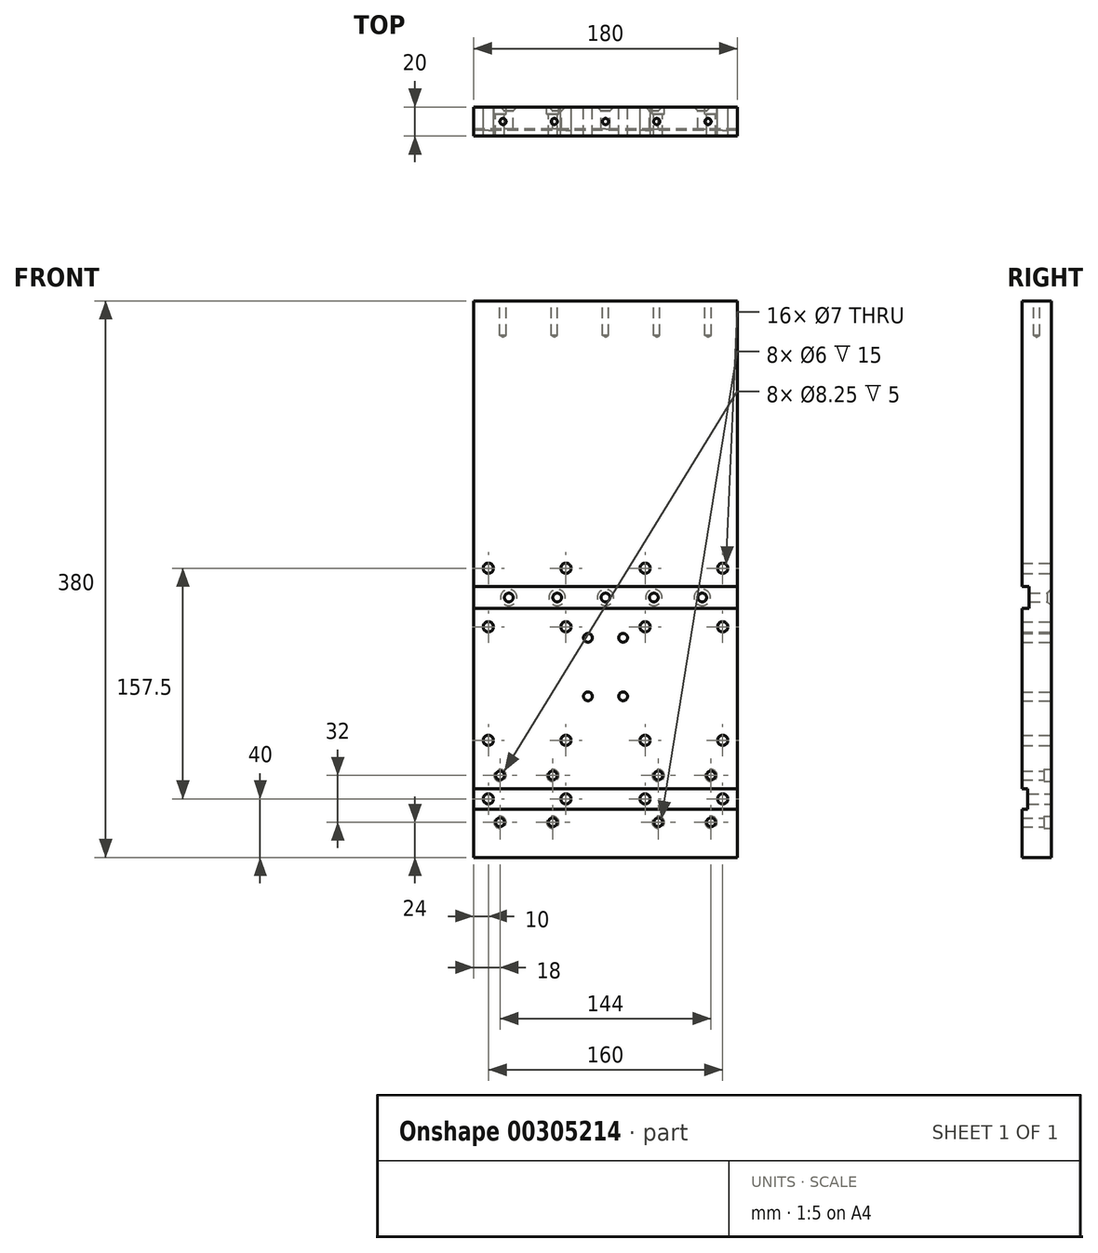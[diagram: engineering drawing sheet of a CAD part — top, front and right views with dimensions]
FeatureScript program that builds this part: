
annotation { "Feature Type Name" : "Feature", "Feature Type Description" : "" }
export const myFeature = defineFeature(function(context is Context, id is Id, definition is map)
    precondition{}
    {
        {
            var Q0;
            Q0=qCreatedBy(makeId("Right.planeOp"),FACE);
            var sketch = newSketch(context, id + "F0", { "sketchPlane" : qUnion([Q0])});
            skLineSegment(sketch, "E0.bottom", {"start": v(0, 0) * mm, "end": v(0, 0) * mm});
            skLineSegment(sketch, "E1.bottom", {"start": v(0, 0) * mm, "end": v(20, 0) * mm});
            skLineSegment(sketch, "E1.top", {"start": v(0, 400) * mm, "end": v(20, 400) * mm});
            skLineSegment(sketch, "E1.left", {"start": v(0, 0) * mm, "end": v(0, 170) * mm});
            skLineSegment(sketch, "E1.right", {"start": v(20, 0) * mm, "end": v(20, 400) * mm});
            skLineSegment(sketch, "E2.0", {"start": v(0, 170) * mm, "end": v(5, 170) * mm});
            skLineSegment(sketch, "E3.0", {"start": v(0, 185) * mm, "end": v(5, 185) * mm});
            skLineSegment(sketch, "E4.0", {"start": v(5, 170) * mm, "end": v(5, 185) * mm});
            skLineSegment(sketch, "E5.trimOffspring", {"start": v(0, 185) * mm, "end": v(0, 400) * mm});
            skSolve(sketch);
        }
        {
            var Q0;
            Q0=makeQuery(id+"F0.imprint","IMPRINT",FACE,{"disambiguationData":[TD([[makeQuery(id+"F0.imprint","IMPRINT",EDGE,{"derivedFrom":sQuery(id+"F0.wireOp",EDGE,"E1.bottom")}),1.0]])]});
            extrude(context, id + "F1", {"entities" : qUnion([Q0]), "depth" : 170 * mm});
        }
        {
            var Q0;
            Q0=makeQuery(id+"F1.opExtrude","SWEPT_FACE",FACE,{"disambiguationData":[OSD([sQuery(id+"F0.wireOp",EDGE,"E1.top")])]});
            extrude(context, id + "F2", {"entities" : qUnion([Q0]), "operationType" : NewBodyOperationType.REMOVE, "oppositeDirection" : true, "depth" : 20 * mm});
        }
        {
            var Q0;
            Q0=makeQuery(id+"F1.opExtrude","SWEPT_FACE",FACE,{"disambiguationData":[OSD([sQuery(id+"F0.wireOp",EDGE,"E1.right")])]});
            var sketch = newSketch(context, id + "F3", { "sketchPlane" : qUnion([Q0])});
            skPoint(sketch, "E6", {"position": v(-165, 40) * mm});
            skPoint(sketch, "E7", {"position": v(-165, 80) * mm});
            skPoint(sketch, "E8", {"position": v(-165, 157.5) * mm});
            skPoint(sketch, "E9", {"position": v(-165, 197.5) * mm});
            skPoint(sketch, "E10", {"position": v(-5, 197.5) * mm});
            skPoint(sketch, "E11", {"position": v(-5, 157.5) * mm});
            skPoint(sketch, "E12", {"position": v(-5, 80) * mm});
            skPoint(sketch, "E13", {"position": v(-5, 40) * mm});
            skPoint(sketch, "E14", {"position": v(-112, 197.5) * mm});
            skPoint(sketch, "E15", {"position": v(-112, 157.5) * mm});
            skPoint(sketch, "E16", {"position": v(-112, 80) * mm});
            skPoint(sketch, "E17", {"position": v(-112, 40) * mm});
            skPoint(sketch, "E18", {"position": v(-58, 197.5) * mm});
            skPoint(sketch, "E19", {"position": v(-58, 157.5) * mm});
            skPoint(sketch, "E20", {"position": v(-58, 80) * mm});
            skPoint(sketch, "E21", {"position": v(-58, 40) * mm});
            skSolve(sketch);
        }
        {
            var Q0;
            Q0=sQuery(id+"F3.wireOp",VERTEX,"E9");
            var Q1;
            Q1=sQuery(id+"F3.wireOp",VERTEX,"E8");
            var Q2;
            Q2=sQuery(id+"F3.wireOp",VERTEX,"E10");
            var Q3;
            Q3=sQuery(id+"F3.wireOp",VERTEX,"E11");
            var Q4;
            Q4=sQuery(id+"F3.wireOp",VERTEX,"E14");
            var Q5;
            Q5=sQuery(id+"F3.wireOp",VERTEX,"E15");
            var Q6;
            Q6=sQuery(id+"F3.wireOp",VERTEX,"E19");
            var Q7;
            Q7=sQuery(id+"F3.wireOp",VERTEX,"E18");
            var Q8;
            Q8=makeQuery(id+"F1.opExtrude","SWEPT_BODY",BODY,{"disambiguationData":[OSD([sQuery(id+"F0.wireOp",EDGE,"E1.bottom"),sQuery(id+"F0.wireOp",EDGE,"E1.top"),sQuery(id+"F0.wireOp",EDGE,"E1.left"),sQuery(id+"F0.wireOp",EDGE,"E1.right"),sQuery(id+"F0.wireOp",EDGE,"E2.0"),sQuery(id+"F0.wireOp",EDGE,"E3.0"),sQuery(id+"F0.wireOp",EDGE,"E4.0"),sQuery(id+"F0.wireOp",EDGE,"E5.trimOffspring")])]});
            hole(context, id + "F4", {"style" : HoleStyle.SIMPLE, "endStyle" : HoleEndStyle.THROUGH, "standardTappedOrClearance" : lookupTablePath({ "standard" : "ISO", "size" : "7", "type" : "Drilled" }), "standardBlindInLast" : lookupTablePath({ "standard" : "ISO", "size" : "7", "type" : "Drilled" }), "holeDiameter" : 7 * mm, "tappedDepth" : 12.6 * mm, "tapClearance" : 3, "startFromSketch" : true, "locations" : qUnion([Q0, Q1, Q2, Q3, Q4, Q5, Q6, Q7]), "scope" : qUnion([Q8])});
        }
        {
            var Q0;
            {var subQ0=sQuery(id+"F0.wireOp",EDGE,"E1.right");Q0=makeQuery(id+"F3.imprint","IMPRINT",FACE,{"disambiguationData":[TD([[makeQuery(id+"F3.imprint","IMPRINT",EDGE,{"derivedFrom":makeQuery(id+"F1.opExtrude","CAP_EDGE",EDGE,{"disambiguationData":[OSD([subQ0])],"isStart":true})}),1.0]])]});}
            var sketch = newSketch(context, id + "F5", { "sketchPlane" : qUnion([Q0])});
            skPoint(sketch, "E22", {"position": v(-151, 177.5) * mm});
            skPoint(sketch, "E23", {"position": v(-19, 177.5) * mm});
            skPoint(sketch, "E24", {"position": v(-85, 177.5) * mm});
            skPoint(sketch, "E25", {"position": v(-118, 177.5) * mm});
            skPoint(sketch, "E26", {"position": v(-52, 177.5) * mm});
            skSolve(sketch);
        }
        {
            var Q0;
            Q0=sQuery(id+"F5.wireOp",VERTEX,"E22");
            var Q1;
            Q1=sQuery(id+"F5.wireOp",VERTEX,"E25");
            var Q2;
            Q2=sQuery(id+"F5.wireOp",VERTEX,"E24");
            var Q3;
            Q3=sQuery(id+"F5.wireOp",VERTEX,"E26");
            var Q4;
            Q4=sQuery(id+"F5.wireOp",VERTEX,"E23");
            var Q5;
            Q5=makeQuery(id+"F1.opExtrude","SWEPT_BODY",BODY,{"disambiguationData":[OSD([sQuery(id+"F0.wireOp",EDGE,"E1.bottom"),sQuery(id+"F0.wireOp",EDGE,"E1.top"),sQuery(id+"F0.wireOp",EDGE,"E1.left"),sQuery(id+"F0.wireOp",EDGE,"E1.right"),sQuery(id+"F0.wireOp",EDGE,"E2.0"),sQuery(id+"F0.wireOp",EDGE,"E3.0"),sQuery(id+"F0.wireOp",EDGE,"E4.0"),sQuery(id+"F0.wireOp",EDGE,"E5.trimOffspring")])]});
            hole(context, id + "F6", {"style" : HoleStyle.C_SINK, "endStyle" : HoleEndStyle.THROUGH, "standardTappedOrClearance" : lookupTablePath({ "standard" : "ISO", "size" : "6", "type" : "Drilled" }), "standardBlindInLast" : lookupTablePath({ "standard" : "ISO", "size" : "6", "type" : "Drilled" }), "holeDiameter" : 6 * mm, "cSinkDiameter" : 11.2 * mm, "cSinkAngle" : 90 * degree, "tappedDepth" : 12.6 * mm, "tapClearance" : 3, "startFromSketch" : true, "locations" : qUnion([Q0, Q1, Q2, Q3, Q4]), "scope" : qUnion([Q5])});
        }
        {
            var Q0;
            Q0=makeQuery(id+"F0.imprint","IMPRINT",FACE,{"disambiguationData":[TD([[makeQuery(id+"F0.imprint","IMPRINT",EDGE,{"derivedFrom":sQuery(id+"F0.wireOp",EDGE,"E1.bottom")}),1.0]])]});
            extrude(context, id + "F7", {"entities" : qUnion([Q0]), "operationType" : NewBodyOperationType.ADD, "oppositeDirection" : true, "depth" : 5 * mm});
        }
        {
            var Q0;
            Q0=makeQuery(id+"F1.opExtrude","CAP_FACE",FACE,{"disambiguationData":[OSD([sQuery(id+"F0.wireOp",EDGE,"E1.bottom"),sQuery(id+"F0.wireOp",EDGE,"E1.top"),sQuery(id+"F0.wireOp",EDGE,"E1.left"),sQuery(id+"F0.wireOp",EDGE,"E1.right"),sQuery(id+"F0.wireOp",EDGE,"E2.0"),sQuery(id+"F0.wireOp",EDGE,"E3.0"),sQuery(id+"F0.wireOp",EDGE,"E4.0"),sQuery(id+"F0.wireOp",EDGE,"E5.trimOffspring")])],"isStart":false});
            extrude(context, id + "F8", {"entities" : qUnion([Q0]), "operationType" : NewBodyOperationType.ADD, "depth" : 5 * mm});
        }
        {
            var Q0;
            Q0=makeQuery(id+"F7.opExtrude","SWEPT_FACE",FACE,{"disambiguationData":[OSD([sQuery(id+"F0.wireOp",EDGE,"E1.top")])]});
            extrude(context, id + "F9", {"entities" : qUnion([Q0]), "operationType" : NewBodyOperationType.REMOVE, "oppositeDirection" : true, "depth" : 20 * mm});
        }
        {
            var Q0;
            Q0=sQuery(id+"F3.wireOp",VERTEX,"E7");
            var Q1;
            Q1=sQuery(id+"F3.wireOp",VERTEX,"E6");
            var Q2;
            Q2=sQuery(id+"F3.wireOp",VERTEX,"E16");
            var Q3;
            Q3=sQuery(id+"F3.wireOp",VERTEX,"E17");
            var Q4;
            Q4=sQuery(id+"F3.wireOp",VERTEX,"E21");
            var Q5;
            Q5=sQuery(id+"F3.wireOp",VERTEX,"E12");
            var Q6;
            Q6=sQuery(id+"F3.wireOp",VERTEX,"E20");
            var Q7;
            Q7=sQuery(id+"F3.wireOp",VERTEX,"E13");
            var Q8;
            Q8=makeQuery(id+"F1.opExtrude","SWEPT_BODY",BODY,{"disambiguationData":[OSD([sQuery(id+"F0.wireOp",EDGE,"E1.bottom"),sQuery(id+"F0.wireOp",EDGE,"E1.top"),sQuery(id+"F0.wireOp",EDGE,"E1.left"),sQuery(id+"F0.wireOp",EDGE,"E1.right"),sQuery(id+"F0.wireOp",EDGE,"E2.0"),sQuery(id+"F0.wireOp",EDGE,"E3.0"),sQuery(id+"F0.wireOp",EDGE,"E4.0"),sQuery(id+"F0.wireOp",EDGE,"E5.trimOffspring")])]});
            hole(context, id + "F10", {"style" : HoleStyle.SIMPLE, "endStyle" : HoleEndStyle.THROUGH, "standardTappedOrClearance" : lookupTablePath({ "standard" : "ISO", "size" : "7", "type" : "Drilled" }), "standardBlindInLast" : lookupTablePath({ "standard" : "ISO", "size" : "7", "type" : "Drilled" }), "holeDiameter" : 7 * mm, "tappedDepth" : 15 * mm, "tapClearance" : 3, "startFromSketch" : true, "locations" : qUnion([Q0, Q1, Q2, Q3, Q4, Q5, Q6, Q7]), "scope" : qUnion([Q8])});
        }
        {
            var Q0;
            {var subQ0=sQuery(id+"F0.wireOp",EDGE,"E1.right");Q0=makeQuery(id+"F3.imprint","IMPRINT",FACE,{"disambiguationData":[TD([[makeQuery(id+"F3.imprint","IMPRINT",EDGE,{"derivedFrom":makeQuery(id+"F1.opExtrude","CAP_EDGE",EDGE,{"disambiguationData":[OSD([subQ0])],"isStart":true})}),1.0]])]});}
            var sketch = newSketch(context, id + "F11", { "sketchPlane" : qUnion([Q0])});
            skPoint(sketch, "E27", {"position": v(-121, 56) * mm});
            skPoint(sketch, "E28", {"position": v(-157, 56) * mm});
            skPoint(sketch, "E29", {"position": v(-157, 24) * mm});
            skPoint(sketch, "E30", {"position": v(-121, 24) * mm});
            skPoint(sketch, "E31", {"position": v(-49, 56) * mm});
            skPoint(sketch, "E32", {"position": v(-49, 24) * mm});
            skPoint(sketch, "E33", {"position": v(-13, 24) * mm});
            skPoint(sketch, "E34", {"position": v(-13, 56) * mm});
            skSolve(sketch);
        }
        {
            var Q0;
            Q0=sQuery(id+"F11.wireOp",VERTEX,"E28");
            var Q1;
            Q1=sQuery(id+"F11.wireOp",VERTEX,"E29");
            var Q2;
            Q2=sQuery(id+"F11.wireOp",VERTEX,"E27");
            var Q3;
            Q3=sQuery(id+"F11.wireOp",VERTEX,"E30");
            var Q4;
            Q4=sQuery(id+"F11.wireOp",VERTEX,"E31");
            var Q5;
            Q5=sQuery(id+"F11.wireOp",VERTEX,"E32");
            var Q6;
            Q6=sQuery(id+"F11.wireOp",VERTEX,"E33");
            var Q7;
            Q7=sQuery(id+"F11.wireOp",VERTEX,"E34");
            var Q8;
            Q8=makeQuery(id+"F1.opExtrude","SWEPT_BODY",BODY,{"disambiguationData":[OSD([sQuery(id+"F0.wireOp",EDGE,"E1.bottom"),sQuery(id+"F0.wireOp",EDGE,"E1.top"),sQuery(id+"F0.wireOp",EDGE,"E1.left"),sQuery(id+"F0.wireOp",EDGE,"E1.right"),sQuery(id+"F0.wireOp",EDGE,"E2.0"),sQuery(id+"F0.wireOp",EDGE,"E3.0"),sQuery(id+"F0.wireOp",EDGE,"E4.0"),sQuery(id+"F0.wireOp",EDGE,"E5.trimOffspring")])]});
            hole(context, id + "F12", {"style" : HoleStyle.C_BORE, "endStyle" : HoleEndStyle.THROUGH, "holeDiameter" : 6 * mm, "cBoreDiameter" : 8.25 * mm, "cBoreDepth" : 5 * mm, "tappedDepth" : 21 * mm, "tapClearance" : 3, "startFromSketch" : true, "locations" : qUnion([Q0, Q1, Q2, Q3, Q4, Q5, Q6, Q7]), "scope" : qUnion([Q8])});
        }
        {
            var Q0;
            {var subQ0=sQuery(id+"F0.wireOp",EDGE,"E1.right");Q0=makeQuery(id+"F3.imprint","IMPRINT",FACE,{"disambiguationData":[TD([[makeQuery(id+"F3.imprint","IMPRINT",EDGE,{"derivedFrom":makeQuery(id+"F1.opExtrude","CAP_EDGE",EDGE,{"disambiguationData":[OSD([subQ0])],"isStart":true})}),1.0]])]});}
            var sketch = newSketch(context, id + "F13", { "sketchPlane" : qUnion([Q0])});
            skPoint(sketch, "E35", {"position": v(-97, 150) * mm});
            skPoint(sketch, "E36", {"position": v(-73, 150) * mm});
            skPoint(sketch, "E37", {"position": v(-73, 110) * mm});
            skPoint(sketch, "E38", {"position": v(-97, 110) * mm});
            skSolve(sketch);
        }
        {
            var Q0;
            Q0=sQuery(id+"F13.wireOp",VERTEX,"E35");
            var Q1;
            Q1=sQuery(id+"F13.wireOp",VERTEX,"E38");
            var Q2;
            Q2=sQuery(id+"F13.wireOp",VERTEX,"E37");
            var Q3;
            Q3=sQuery(id+"F13.wireOp",VERTEX,"E36");
            var Q4;
            Q4=makeQuery(id+"F1.opExtrude","SWEPT_BODY",BODY,{"disambiguationData":[OSD([sQuery(id+"F0.wireOp",EDGE,"E1.bottom"),sQuery(id+"F0.wireOp",EDGE,"E1.top"),sQuery(id+"F0.wireOp",EDGE,"E1.left"),sQuery(id+"F0.wireOp",EDGE,"E1.right"),sQuery(id+"F0.wireOp",EDGE,"E2.0"),sQuery(id+"F0.wireOp",EDGE,"E3.0"),sQuery(id+"F0.wireOp",EDGE,"E4.0"),sQuery(id+"F0.wireOp",EDGE,"E5.trimOffspring")])]});
            hole(context, id + "F14", {"style" : HoleStyle.SIMPLE, "endStyle" : HoleEndStyle.THROUGH, "holeDiameter" : 6 * mm, "tappedDepth" : 12 * mm, "tapClearance" : 3, "startFromSketch" : true, "locations" : qUnion([Q0, Q1, Q2, Q3]), "scope" : qUnion([Q4])});
        }
        {
            var Q0;
            {var subQ0=sQuery(id+"F0.wireOp",EDGE,"E1.top");Q0=makeQuery(id+"F9.boolean.opBoolean","MERGE",FACE,{"derivedFrom":[makeQuery(id+"F8.boolean.opBoolean","MERGE",FACE,{"derivedFrom":[makeQuery(id+"F2.boolean.opBoolean","COPY",FACE,{"derivedFrom":makeQuery(id+"F2.opExtrude","CAP_FACE",FACE,{"disambiguationData":[OSD([subQ0])],"isStart":false})}),makeQuery(id+"F8.opExtrude","SWEPT_FACE",FACE,{"disambiguationData":[OSD([subQ0])]})]}),makeQuery(id+"F9.opExtrude","CAP_FACE",FACE,{"disambiguationData":[OSD([subQ0])],"isStart":false})]});}
            var sketch = newSketch(context, id + "F15", { "sketchPlane" : qUnion([Q0])});
            skPoint(sketch, "E39", {"position": v(15, 10) * mm});
            skPoint(sketch, "E40", {"position": v(50, 10) * mm});
            skPoint(sketch, "E41", {"position": v(85, 10) * mm});
            skPoint(sketch, "E42", {"position": v(120, 10) * mm});
            skPoint(sketch, "E43", {"position": v(155, 10) * mm});
            skSolve(sketch);
        }
        {
            var Q0;
            Q0=sQuery(id+"F15.wireOp",VERTEX,"E39");
            var Q1;
            Q1=sQuery(id+"F15.wireOp",VERTEX,"E40");
            var Q2;
            Q2=sQuery(id+"F15.wireOp",VERTEX,"E41");
            var Q3;
            Q3=sQuery(id+"F15.wireOp",VERTEX,"E42");
            var Q4;
            Q4=sQuery(id+"F15.wireOp",VERTEX,"E43");
            var Q5;
            Q5=makeQuery(id+"F1.opExtrude","SWEPT_BODY",BODY,{"disambiguationData":[OSD([sQuery(id+"F0.wireOp",EDGE,"E1.bottom"),sQuery(id+"F0.wireOp",EDGE,"E1.top"),sQuery(id+"F0.wireOp",EDGE,"E1.left"),sQuery(id+"F0.wireOp",EDGE,"E1.right"),sQuery(id+"F0.wireOp",EDGE,"E2.0"),sQuery(id+"F0.wireOp",EDGE,"E3.0"),sQuery(id+"F0.wireOp",EDGE,"E4.0"),sQuery(id+"F0.wireOp",EDGE,"E5.trimOffspring")])]});
            hole(context, id + "F16", {"style" : HoleStyle.SIMPLE, "endStyle" : HoleEndStyle.BLIND, "standardTappedOrClearance" : lookupTablePath({ "standard" : "ISO", "engagement" : "75%", "pitch" : "0.8 mm", "size" : "M5", "type" : "Tapped" }), "standardBlindInLast" : lookupTablePath({ "standard" : "ISO", "engagement" : "75%", "pitch" : "0.8 mm", "size" : "M5", "type" : "Tapped" }), "holeDiameter" : 4.2 * mm, "showTappedDepth" : true, "holeDepth" : 23.4 * mm, "isTappedThrough" : true, "tappedDepth" : 21 * mm, "tapClearance" : 3, "startFromSketch" : true, "locations" : qUnion([Q0, Q1, Q2, Q3, Q4]), "scope" : qUnion([Q5]), "majorDiameter" : 5 * mm});
        }
        {
            var Q0;
            {var subQ0=sQuery(id+"F0.wireOp",EDGE,"E1.left");Q0=makeQuery(id+"F8.boolean.opBoolean","MERGE",FACE,{"derivedFrom":[makeQuery(id+"F7.boolean.opBoolean","MERGE",FACE,{"derivedFrom":[makeQuery(id+"F1.opExtrude","SWEPT_FACE",FACE,{"disambiguationData":[OSD([subQ0])]}),makeQuery(id+"F7.opExtrude","SWEPT_FACE",FACE,{"disambiguationData":[OSD([subQ0])]})]}),makeQuery(id+"F8.opExtrude","SWEPT_FACE",FACE,{"disambiguationData":[OSD([subQ0])]})]});}
            var sketch = newSketch(context, id + "F17", { "sketchPlane" : qUnion([Q0])});
            skLineSegment(sketch, "E44.0", {"start": v(175, 47) * mm, "end": v(-5, 47) * mm});
            skLineSegment(sketch, "E45.0", {"start": v(175, 33) * mm, "end": v(-5, 33) * mm});
            skLineSegment(sketch, "E46.0", {"start": v(175, 33) * mm, "end": v(175, 47) * mm});
            skLineSegment(sketch, "E47.0", {"start": v(-5, 33) * mm, "end": v(-5, 47) * mm});
            skPoint(sketch, "E48.orphan", {"position": v(-5, 0) * mm});
            skPoint(sketch, "E49.orphan", {"position": v(-5, 170) * mm});
            skPoint(sketch, "E50.orphan", {"position": v(175, 0) * mm});
            skPoint(sketch, "E51.orphan", {"position": v(175, 380) * mm});
            skSolve(sketch);
        }
        {
            var Q0;
            Q0=makeQuery(id+"F17.imprint","IMPRINT",FACE,{"disambiguationData":[TD([[makeQuery(id+"F17.imprint","IMPRINT",EDGE,{"derivedFrom":sQuery(id+"F17.wireOp",EDGE,"E44.0")}),1.0]])]});
            extrude(context, id + "F18", {"entities" : qUnion([Q0]), "operationType" : NewBodyOperationType.REMOVE, "oppositeDirection" : true, "depth" : 4 * mm});
        }
    });
